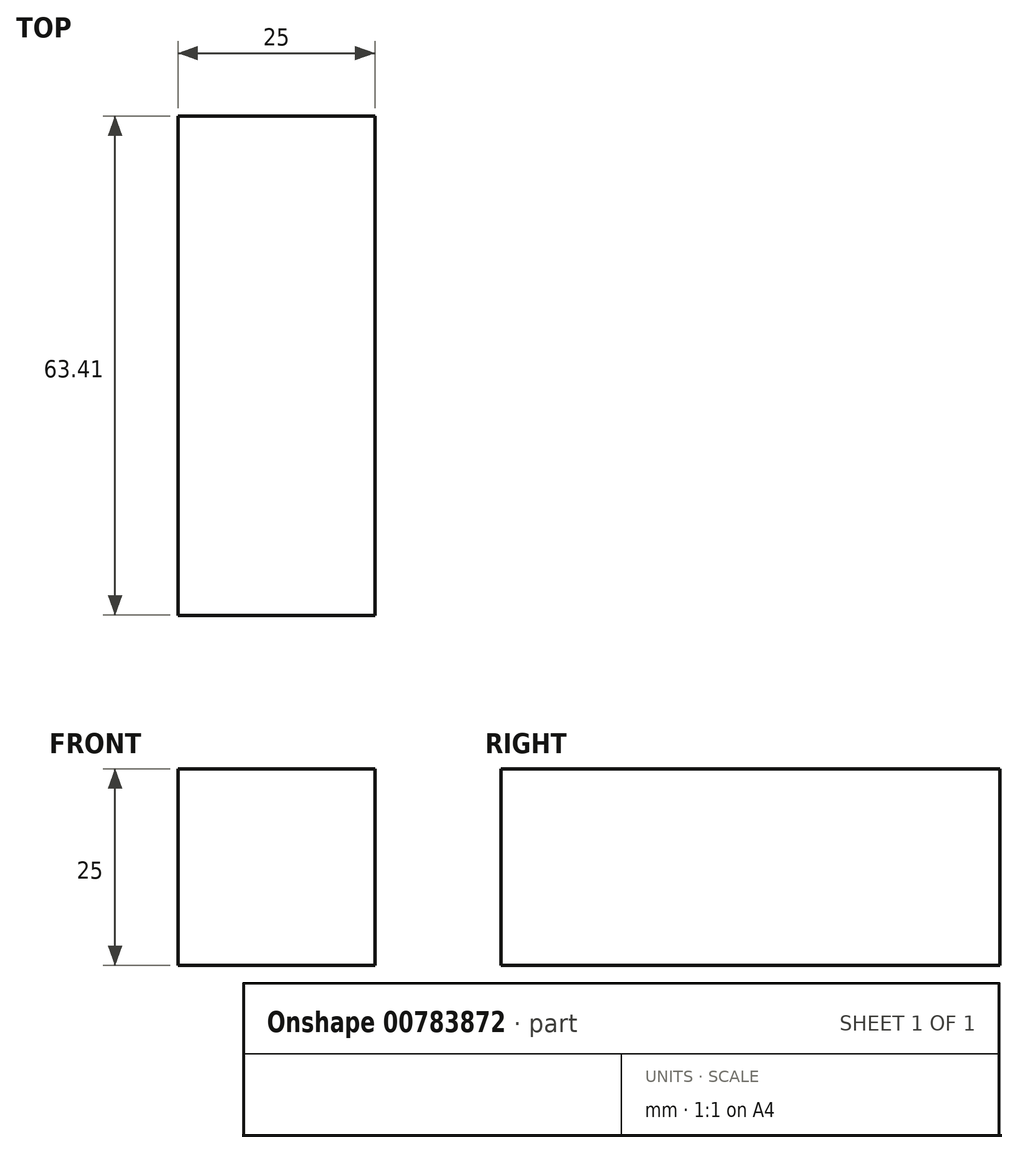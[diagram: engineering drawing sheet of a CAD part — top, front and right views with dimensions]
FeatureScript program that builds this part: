
annotation { "Feature Type Name" : "Feature", "Feature Type Description" : "" }
export const myFeature = defineFeature(function(context is Context, id is Id, definition is map)
    precondition{}
    {
        {
            var Q0;
            Q0=qCreatedBy(makeId("Right.planeOp"),FACE);
            var sketch = newSketch(context, id + "F0", { "sketchPlane" : qUnion([Q0])});
            skLineSegment(sketch, "E0.bottom", {"start": v(-63.41, 83.93) * mm, "end": v(0, 83.93) * mm});
            skLineSegment(sketch, "E0.top", {"start": v(-63.41, 24.98) * mm, "end": v(0, 24.98) * mm});
            skLineSegment(sketch, "E0.left", {"start": v(-63.41, 83.93) * mm, "end": v(-63.41, 24.98) * mm});
            skLineSegment(sketch, "E0.right", {"start": v(0, 83.93) * mm, "end": v(0, 24.98) * mm});
            skSolve(sketch);
        }
        {
            var Q0;
            Q0=sQuery(id+"F0.wireOp",EDGE,"E0.bottom");
            extrude(context, id + "F1", {"bodyType" : ToolBodyType.SURFACE, "surfaceEntities" : qUnion([Q0]), "depth" : 25 * mm, "offsetDistance" : 25 * mm});
        }
        {
            var Q0;
            Q0=makeQuery(id+"F1.opExtrude","SWEPT_FACE",FACE,{"disambiguationData":[OSD([sQuery(id+"F0.wireOp",EDGE,"E0.bottom")])]});
            extrude(context, id + "F2", {"entities" : qUnion([Q0]), "depth" : 25 * mm, "offsetDistance" : 25 * mm});
        }
    });
